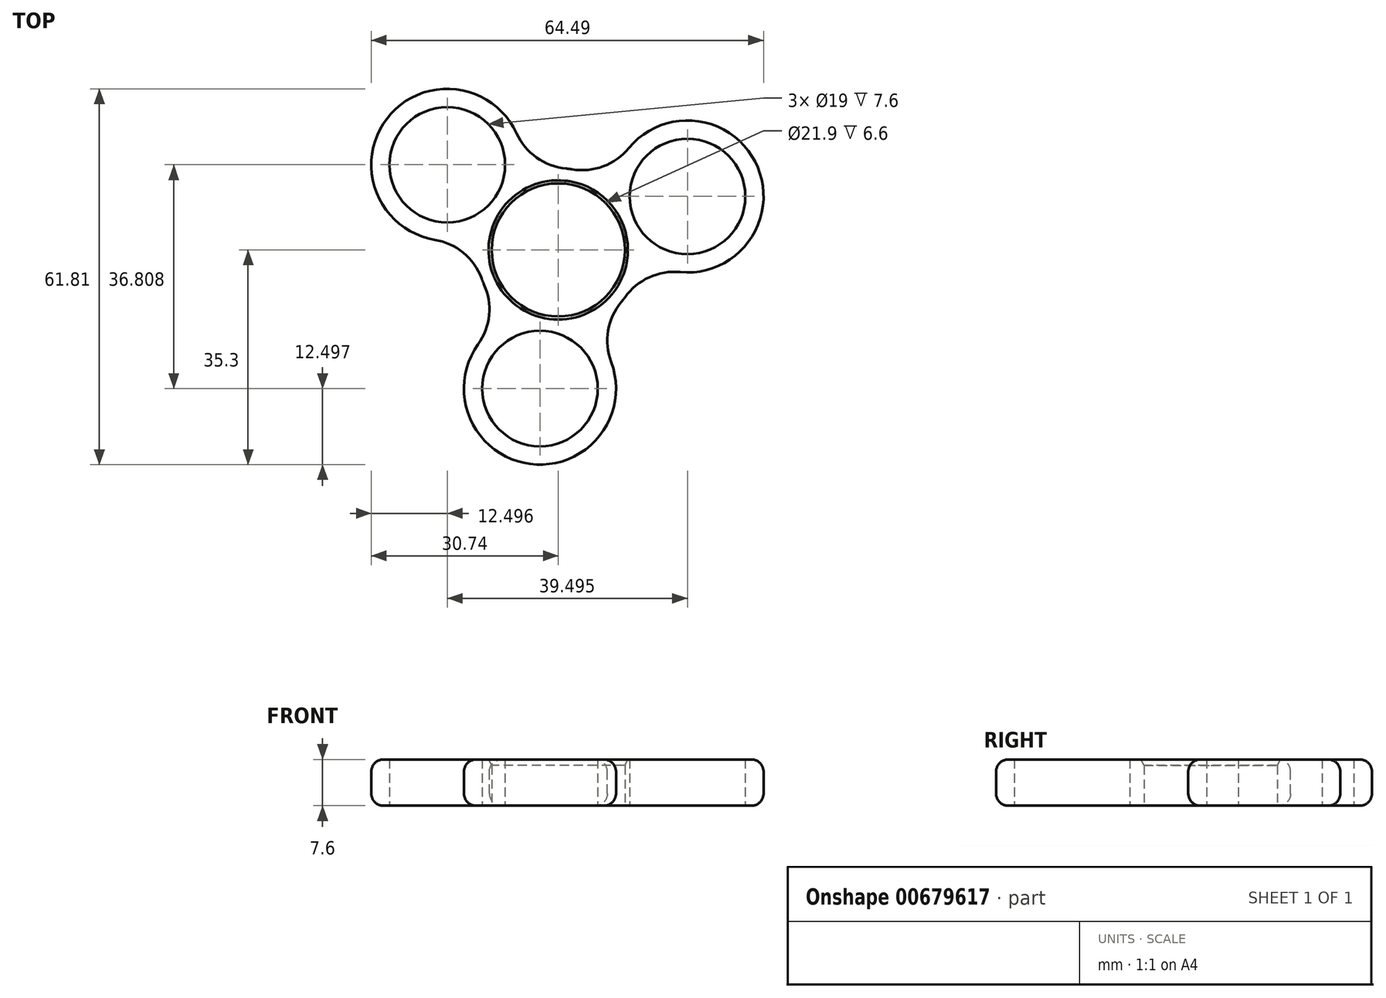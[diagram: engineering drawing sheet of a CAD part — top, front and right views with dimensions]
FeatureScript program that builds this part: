
annotation { "Feature Type Name" : "Feature", "Feature Type Description" : "" }
export const myFeature = defineFeature(function(context is Context, id is Id, definition is map)
    precondition{}
    {
        {
            var Q0;
            Q0=qCreatedBy(makeId("Top.planeOp"),FACE);
            var sketch = newSketch(context, id + "F0", { "sketchPlane" : qUnion([Q0])});
            skCircle(sketch, "E0", {"center": v(0, 0) * mm, "radius": 10.95 * mm});
            skCircle(sketch, "E1.0", {"center": v(0, 0) * mm, "radius": 13.45 * mm});
            skCircle(sketch, "E2.cCircle", {"center": v(0, 0) * mm, "radius": 11.5 * mm, "construction": true});
            skLineSegment(sketch, "E2.0", {"start": v(-18.24, 14) * mm, "end": v(21.25, 8.8) * mm, "construction": true});
            skLineSegment(sketch, "E2.1", {"start": v(21.25, 8.8) * mm, "end": v(-3, -22.8) * mm, "construction": true});
            skLineSegment(sketch, "E2.2", {"start": v(-3, -22.8) * mm, "end": v(-18.24, 14) * mm, "construction": true});
            skPoint(sketch, "E2.0.midPoint", {"position": v(1.5, 11.4) * mm});
            skCircle(sketch, "E3", {"center": v(-18.24, 14) * mm, "radius": 9.5 * mm});
            skCircle(sketch, "E4", {"center": v(21.25, 8.8) * mm, "radius": 9.5 * mm});
            skCircle(sketch, "E5", {"center": v(-3, -22.8) * mm, "radius": 9.5 * mm});
            skCircle(sketch, "E6.0", {"center": v(-18.24, 14) * mm, "radius": 12.5 * mm});
            skCircle(sketch, "E7.0", {"center": v(21.25, 8.8) * mm, "radius": 12.5 * mm});
            skCircle(sketch, "E8.0", {"center": v(-3, -22.8) * mm, "radius": 12.5 * mm});
            skSolve(sketch);
        }
        {
            var Q0;
            Q0=qSketchRegion(id+"F0",true);
            extrude(context, id + "F1", {"entities" : qUnion([Q0]), "depth" : 7.6 * mm, "offsetDistance" : 25 * mm});
        }
        {
            var Q0;
            {var subQ0=sQuery(id+"F0.wireOp",EDGE,"E6.0");var subQ1=sQuery(id+"F0.wireOp",EDGE,"E1.0");Q0=makeQuery(id+"F1.opExtrude","SWEPT_EDGE",EDGE,{"disambiguationData":[OSD([subQ1,subQ0]),TDD([makeQuery(id+"F0.imprint","INTERSECT",VERTEX,{"disambiguationData":[OD(1.0)],"derivedFrom":[subQ1,subQ0]})])]});}
            var Q1;
            {var subQ0=sQuery(id+"F0.wireOp",EDGE,"E6.0");var subQ1=sQuery(id+"F0.wireOp",EDGE,"E1.0");Q1=makeQuery(id+"F1.opExtrude","SWEPT_EDGE",EDGE,{"disambiguationData":[OSD([subQ1,subQ0]),TDD([makeQuery(id+"F0.imprint","INTERSECT",VERTEX,{"disambiguationData":[OD(0.0)],"derivedFrom":[subQ1,subQ0]})])]});}
            var Q2;
            {var subQ0=sQuery(id+"F0.wireOp",EDGE,"E7.0");var subQ1=sQuery(id+"F0.wireOp",EDGE,"E1.0");Q2=makeQuery(id+"F1.opExtrude","SWEPT_EDGE",EDGE,{"disambiguationData":[OSD([subQ1,subQ0]),TDD([makeQuery(id+"F0.imprint","INTERSECT",VERTEX,{"disambiguationData":[OD(0.0)],"derivedFrom":[subQ1,subQ0]})])]});}
            var Q3;
            {var subQ0=sQuery(id+"F0.wireOp",EDGE,"E7.0");var subQ1=sQuery(id+"F0.wireOp",EDGE,"E1.0");Q3=makeQuery(id+"F1.opExtrude","SWEPT_EDGE",EDGE,{"disambiguationData":[OSD([subQ1,subQ0]),TDD([makeQuery(id+"F0.imprint","INTERSECT",VERTEX,{"disambiguationData":[OD(1.0)],"derivedFrom":[subQ1,subQ0]})])]});}
            var Q4;
            {var subQ0=sQuery(id+"F0.wireOp",EDGE,"E8.0");var subQ1=sQuery(id+"F0.wireOp",EDGE,"E1.0");Q4=makeQuery(id+"F1.opExtrude","SWEPT_EDGE",EDGE,{"disambiguationData":[OSD([subQ1,subQ0]),TDD([makeQuery(id+"F0.imprint","INTERSECT",VERTEX,{"disambiguationData":[OD(1.0)],"derivedFrom":[subQ1,subQ0]})])]});}
            var Q5;
            {var subQ0=sQuery(id+"F0.wireOp",EDGE,"E8.0");var subQ1=sQuery(id+"F0.wireOp",EDGE,"E1.0");Q5=makeQuery(id+"F1.opExtrude","SWEPT_EDGE",EDGE,{"disambiguationData":[OSD([subQ1,subQ0]),TDD([makeQuery(id+"F0.imprint","INTERSECT",VERTEX,{"disambiguationData":[OD(0.0)],"derivedFrom":[subQ1,subQ0]})])]});}
            fillet(context, id + "F2", {"entities" : qUnion([Q0, Q1, Q2, Q3, Q4, Q5]), "radius" : 10 * mm, "tangentPropagation" : true, "allowEdgeOverflow" : false});
        }
        {
            var Q0;
            {var subQ0=sQuery(id+"F0.wireOp",EDGE,"E7.0");var subQ1=sQuery(id+"F0.wireOp",EDGE,"E1.0");Q0=makeQuery(id+"F2.opFillet","BLEND_EDGE",EDGE,{"blendedFrom":[makeQuery(id+"F1.opExtrude","SWEPT_EDGE",EDGE,{"disambiguationData":[OSD([subQ1,subQ0]),TDD([makeQuery(id+"F0.imprint","INTERSECT",VERTEX,{"disambiguationData":[OD(1.0)],"derivedFrom":[subQ1,subQ0]})])]}),makeQuery(id+"F1.opExtrude","CAP_FACE",FACE,{"disambiguationData":[OSD([sQuery(id+"F0.wireOp",EDGE,"E0"),subQ1,sQuery(id+"F0.wireOp",EDGE,"E3"),sQuery(id+"F0.wireOp",EDGE,"E4"),sQuery(id+"F0.wireOp",EDGE,"E5"),sQuery(id+"F0.wireOp",EDGE,"E6.0"),subQ0,sQuery(id+"F0.wireOp",EDGE,"E8.0")])],"isStart":true})],"blendedInto":[makeQuery(id+"F1.opExtrude","CAP_FACE",FACE,{"disambiguationData":[OSD([sQuery(id+"F0.wireOp",EDGE,"E0"),subQ1,sQuery(id+"F0.wireOp",EDGE,"E3"),sQuery(id+"F0.wireOp",EDGE,"E4"),sQuery(id+"F0.wireOp",EDGE,"E5"),sQuery(id+"F0.wireOp",EDGE,"E6.0"),subQ0,sQuery(id+"F0.wireOp",EDGE,"E8.0")])],"isStart":true})]});}
            var Q1;
            {var subQ0=sQuery(id+"F0.wireOp",EDGE,"E8.0");var subQ1=sQuery(id+"F0.wireOp",EDGE,"E1.0");Q1=makeQuery(id+"F2.opFillet","BLEND_EDGE",EDGE,{"blendedFrom":[makeQuery(id+"F1.opExtrude","SWEPT_EDGE",EDGE,{"disambiguationData":[OSD([subQ1,subQ0]),TDD([makeQuery(id+"F0.imprint","INTERSECT",VERTEX,{"disambiguationData":[OD(0.0)],"derivedFrom":[subQ1,subQ0]})])]}),makeQuery(id+"F1.opExtrude","CAP_FACE",FACE,{"disambiguationData":[OSD([sQuery(id+"F0.wireOp",EDGE,"E0"),subQ1,sQuery(id+"F0.wireOp",EDGE,"E3"),sQuery(id+"F0.wireOp",EDGE,"E4"),sQuery(id+"F0.wireOp",EDGE,"E5"),sQuery(id+"F0.wireOp",EDGE,"E6.0"),sQuery(id+"F0.wireOp",EDGE,"E7.0"),subQ0])],"isStart":false})],"blendedInto":[makeQuery(id+"F1.opExtrude","CAP_FACE",FACE,{"disambiguationData":[OSD([sQuery(id+"F0.wireOp",EDGE,"E0"),subQ1,sQuery(id+"F0.wireOp",EDGE,"E3"),sQuery(id+"F0.wireOp",EDGE,"E4"),sQuery(id+"F0.wireOp",EDGE,"E5"),sQuery(id+"F0.wireOp",EDGE,"E6.0"),sQuery(id+"F0.wireOp",EDGE,"E7.0"),subQ0])],"isStart":false})]});}
            fillet(context, id + "F3", {"entities" : qUnion([Q0, Q1]), "radius" : 2 * mm, "tangentPropagation" : true, "allowEdgeOverflow" : false});
        }
        {
            var Q0;
            Q0=makeQuery(id+"F1.opExtrude","CAP_EDGE",EDGE,{"disambiguationData":[OSD([sQuery(id+"F0.wireOp",EDGE,"E0")])],"isStart":false});
            chamfer(context, id + "F4", {"entities" : qUnion([Q0]), "chamferType" : ChamferType.TWO_OFFSETS, "width1" : 1 * mm, "oppositeDirection" : false, "width2" : .5 * mm, "tangentPropagation" : true});
        }
    });
